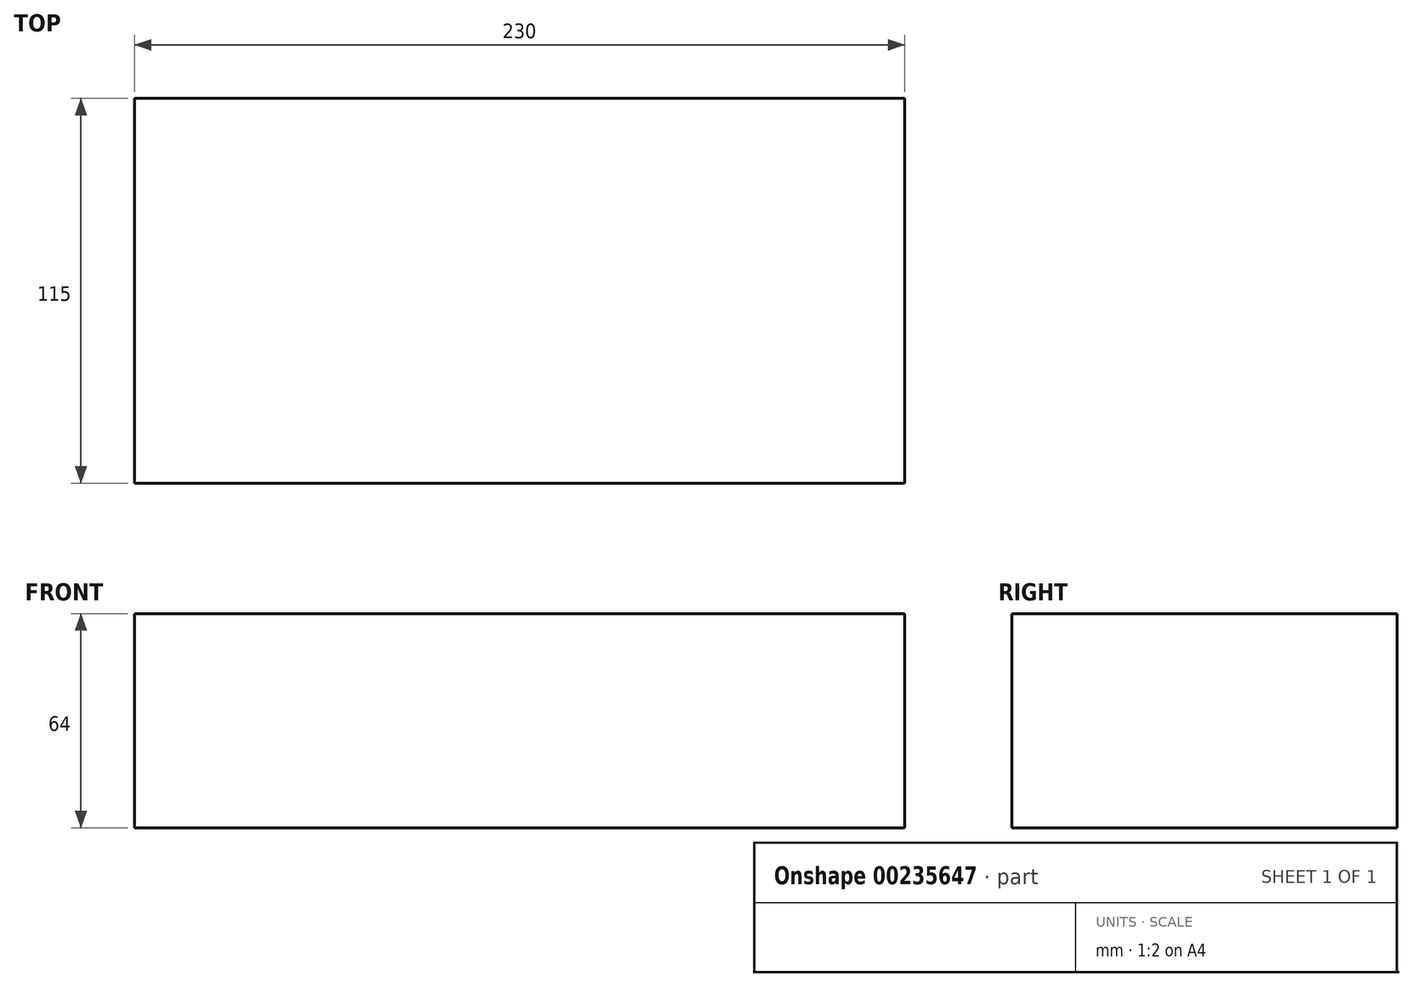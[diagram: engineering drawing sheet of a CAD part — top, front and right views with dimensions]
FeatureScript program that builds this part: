
annotation { "Feature Type Name" : "Feature", "Feature Type Description" : "" }
export const myFeature = defineFeature(function(context is Context, id is Id, definition is map)
    precondition{}
    {
        {
            var Q0;
            Q0=qCreatedBy(makeId("Top.planeOp"),FACE);
            var sketch = newSketch(context, id + "F0", { "sketchPlane" : qUnion([Q0])});
            skLineSegment(sketch, "E0.bottom", {"start": v(115, -57.5) * mm, "end": v(-115, -57.5) * mm});
            skLineSegment(sketch, "E0.top", {"start": v(115, 57.5) * mm, "end": v(-115, 57.5) * mm});
            skLineSegment(sketch, "E0.left", {"start": v(115, -57.5) * mm, "end": v(115, 57.5) * mm});
            skLineSegment(sketch, "E0.right", {"start": v(-115, -57.5) * mm, "end": v(-115, 57.5) * mm});
            skPoint(sketch, "E0.middle", {"position": v(0, 0) * mm});
            skSolve(sketch);
        }
        {
            var Q0;
            Q0 = qSketchRegion(id + "F0", true);
            extrude(context, id + "F1", {"entities" : qUnion([Q0]), "depth" : 64 * mm});
        }
    });
